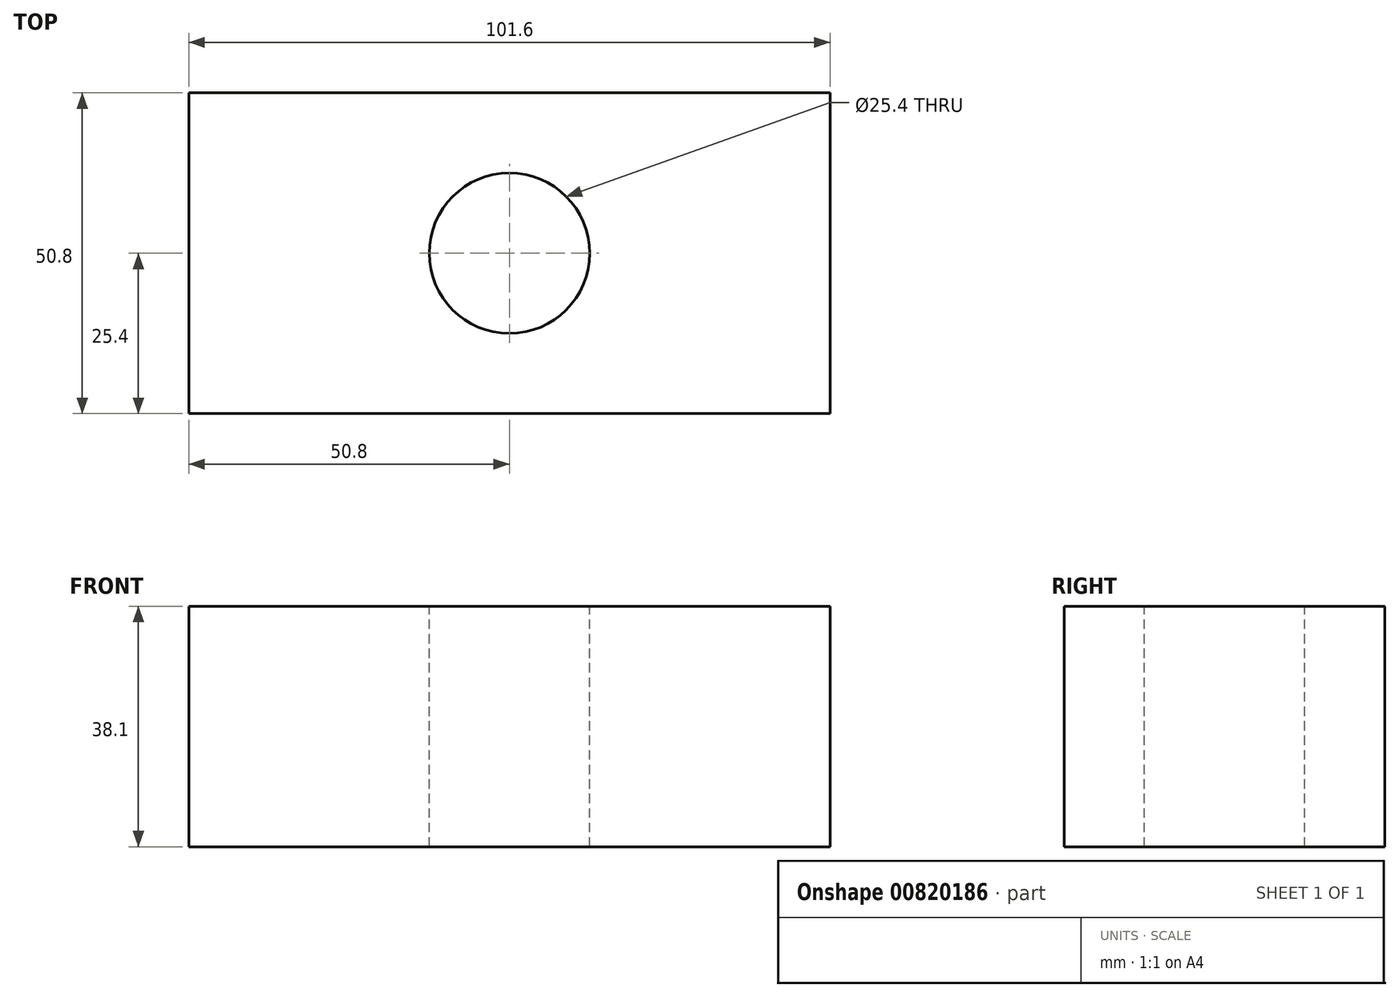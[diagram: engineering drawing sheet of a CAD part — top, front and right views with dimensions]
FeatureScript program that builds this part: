
annotation { "Feature Type Name" : "Feature", "Feature Type Description" : "" }
export const myFeature = defineFeature(function(context is Context, id is Id, definition is map)
    precondition{}
    {
        {
            var Q0;
            Q0=qCreatedBy(makeId("Top.planeOp"),FACE);
            var sketch = newSketch(context, id + "F0", { "sketchPlane" : qUnion([Q0])});
            skLineSegment(sketch, "E0.bottom", {"start": v(-50.8, 25.4) * mm, "end": v(50.8, 25.4) * mm});
            skLineSegment(sketch, "E0.top", {"start": v(-50.8, -25.4) * mm, "end": v(50.8, -25.4) * mm});
            skLineSegment(sketch, "E0.left", {"start": v(-50.8, 25.4) * mm, "end": v(-50.8, -25.4) * mm});
            skLineSegment(sketch, "E0.right", {"start": v(50.8, 25.4) * mm, "end": v(50.8, -25.4) * mm});
            skSolve(sketch);
        }
        {
            var Q0;
            Q0=makeQuery(id+"F0.imprint","IMPRINT",FACE,{"disambiguationData":[TD([[makeQuery(id+"F0.imprint","IMPRINT",EDGE,{"derivedFrom":sQuery(id+"F0.wireOp",EDGE,"E0.bottom")}),-1.0]])]});
            extrude(context, id + "F1", {"entities" : qUnion([Q0]), "endBound" : BoundingType.SYMMETRIC, "depth" : 38.1 * mm, "offsetDistance" : 25.4 * mm});
        }
        {
            var Q0;
            Q0=makeQuery(id+"F1.opExtrude","CAP_FACE",FACE,{"disambiguationData":[OSD([sQuery(id+"F0.wireOp",EDGE,"E0.bottom"),sQuery(id+"F0.wireOp",EDGE,"E0.top"),sQuery(id+"F0.wireOp",EDGE,"E0.left"),sQuery(id+"F0.wireOp",EDGE,"E0.right")])],"isStart":false});
            var sketch = newSketch(context, id + "F2", { "sketchPlane" : qUnion([Q0])});
            skCircle(sketch, "E1", {"center": v(0, 0) * mm, "radius": 12.7 * mm});
            skSolve(sketch);
        }
        {
            var Q0;
            Q0=makeQuery(id+"F2.imprint","IMPRINT",FACE,{"disambiguationData":[TD([[makeQuery(id+"F2.imprint","IMPRINT",EDGE,{"derivedFrom":sQuery(id+"F2.wireOp",EDGE,"E1")}),1.0]])]});
            extrude(context, id + "F3", {"entities" : qUnion([Q0]), "operationType" : NewBodyOperationType.REMOVE, "endBound" : BoundingType.THROUGH_ALL, "oppositeDirection" : true, "depth" : 25.4 * mm, "offsetDistance" : 25.4 * mm});
        }
    });
